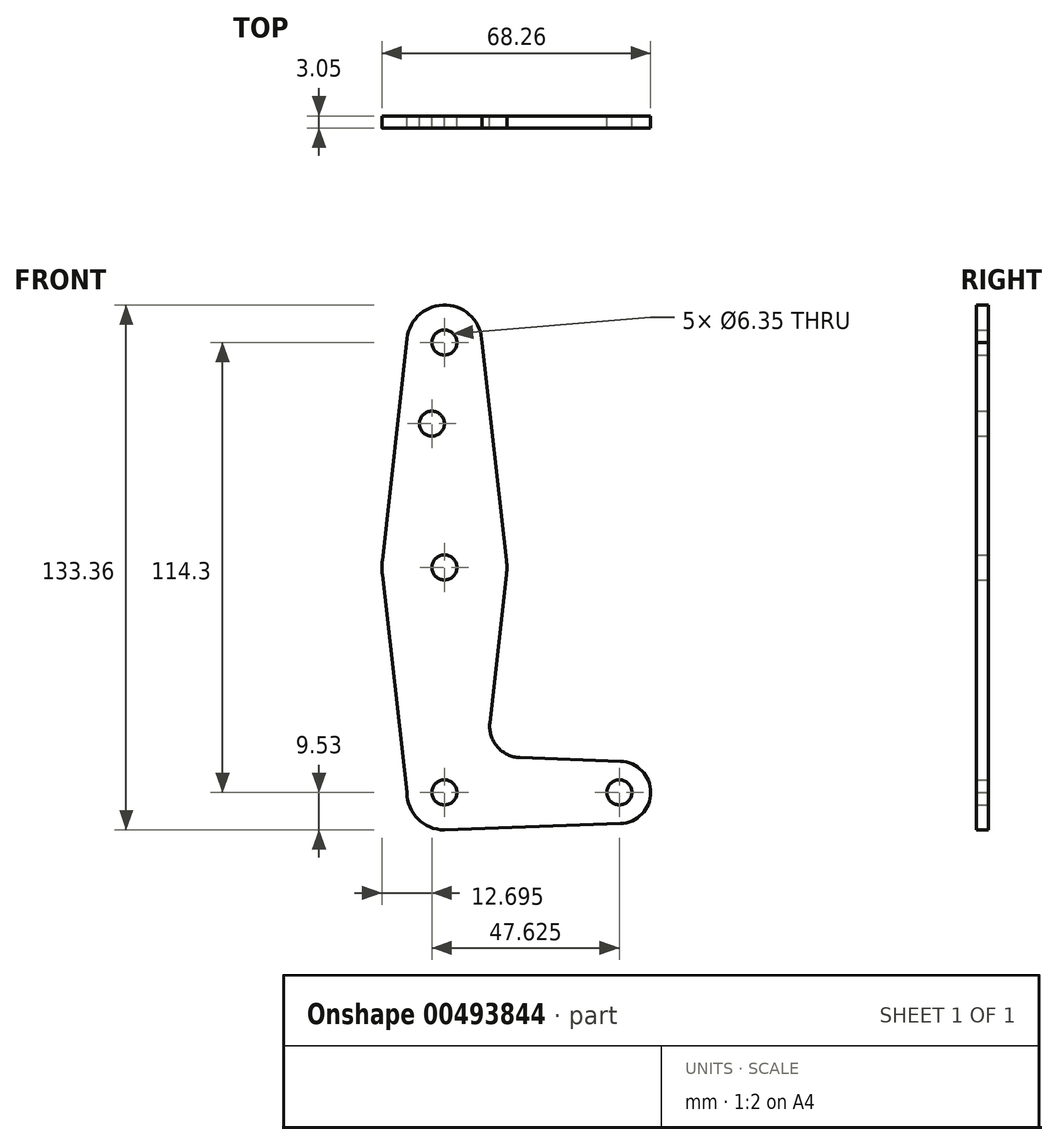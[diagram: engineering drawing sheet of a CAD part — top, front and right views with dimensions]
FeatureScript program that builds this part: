
annotation { "Feature Type Name" : "Feature", "Feature Type Description" : "" }
export const myFeature = defineFeature(function(context is Context, id is Id, definition is map)
    precondition{}
    {
        {
            var Q0;
            Q0=qCreatedBy(makeId("Front.planeOp"),FACE);
            var sketch = newSketch(context, id + "F0", { "sketchPlane" : qUnion([Q0])});
            skLineSegment(sketch, "E0", {"start": v(0, 0) * mm, "end": v(0, 114.3) * mm, "construction": true});
            skLineSegment(sketch, "E1", {"start": v(0, 0) * mm, "end": v(44.45, 0) * mm, "construction": true});
            skCircle(sketch, "E2", {"center": v(0, 114.3) * mm, "radius": 9.53 * mm});
            skCircle(sketch, "E3", {"center": v(0, 0) * mm, "radius": 9.53 * mm});
            skCircle(sketch, "E4", {"center": v(44.45, 0) * mm, "radius": 7.94 * mm});
            skCircle(sketch, "E5", {"center": v(0, 57.15) * mm, "radius": 15.88 * mm});
            skLineSegment(sketch, "E6", {"start": v(9.53, 114.3) * mm, "end": v(15.77, 58.93) * mm});
            skLineSegment(sketch, "E7", {"start": v(-9.52, 0) * mm, "end": v(-15.77, 55.37) * mm});
            skLineSegment(sketch, "E8", {"start": v(19.18, 8.84) * mm, "end": v(44.73, 7.93) * mm});
            skLineSegment(sketch, "E9", {"start": v(0, -9.53) * mm, "end": v(44.73, -7.93) * mm});
            skLineSegment(sketch, "E10", {"start": v(-9.47, 115.36) * mm, "end": v(-15.77, 58.93) * mm});
            skLineSegment(sketch, "E11", {"start": v(15.77, 55.37) * mm, "end": v(11.56, 17.67) * mm});
            skCircle(sketch, "E12", {"center": v(0, 114.3) * mm, "radius": 3.18 * mm});
            skCircle(sketch, "E13", {"center": v(0, 57.15) * mm, "radius": 3.18 * mm});
            skCircle(sketch, "E14", {"center": v(0, 0) * mm, "radius": 3.18 * mm});
            skCircle(sketch, "E15", {"center": v(44.45, 0) * mm, "radius": 3.18 * mm});
            skCircle(sketch, "E16", {"center": v(-3.18, 93.68) * mm, "radius": 3.18 * mm});
            skArc(sketch, "E17.filletArc", {"start": v(11.56, 17.67) * mm, "mid": v(13.44, 11.6) * mm, "end": v(19.18, 8.84) * mm});
            skSolve(sketch);
        }
        {
            var Q0;
            {var subQ0=sQuery(id+"F0.wireOp",EDGE,"E6");Q0=makeQuery(id+"F0.imprint","IMPRINT",FACE,{"disambiguationData":[TD([[makeQuery(id+"F0.imprint","IMPRINT",EDGE,{"derivedFrom":subQ0}),-1.0]])]});}
            var Q1;
            Q1=makeQuery(id+"F0.imprint","IMPRINT",FACE,{"disambiguationData":[TD([[makeQuery(id+"F0.imprint","IMPRINT",EDGE,{"derivedFrom":sQuery(id+"F0.wireOp",EDGE,"E12")}),-1.0]])]});
            var Q2;
            Q2=makeQuery(id+"F0.imprint","IMPRINT",FACE,{"disambiguationData":[TD([[makeQuery(id+"F0.imprint","IMPRINT",EDGE,{"derivedFrom":sQuery(id+"F0.wireOp",EDGE,"E13")}),-1.0]])]});
            var Q3;
            {var subQ0=sQuery(id+"F0.wireOp",EDGE,"E7");Q3=makeQuery(id+"F0.imprint","IMPRINT",FACE,{"disambiguationData":[TD([[makeQuery(id+"F0.imprint","IMPRINT",EDGE,{"derivedFrom":subQ0}),-1.0]])]});}
            var Q4;
            Q4=makeQuery(id+"F0.imprint","IMPRINT",FACE,{"disambiguationData":[TD([[makeQuery(id+"F0.imprint","IMPRINT",EDGE,{"derivedFrom":sQuery(id+"F0.wireOp",EDGE,"E14")}),-1.0]])]});
            var Q5;
            Q5=makeQuery(id+"F0.imprint","IMPRINT",FACE,{"disambiguationData":[TD([[makeQuery(id+"F0.imprint","IMPRINT",EDGE,{"derivedFrom":sQuery(id+"F0.wireOp",EDGE,"E15")}),-1.0]])]});
            extrude(context, id + "F1", {"entities" : qUnion([Q0, Q1, Q2, Q3, Q4, Q5]), "depth" : 3.05 * mm});
        }
    });
